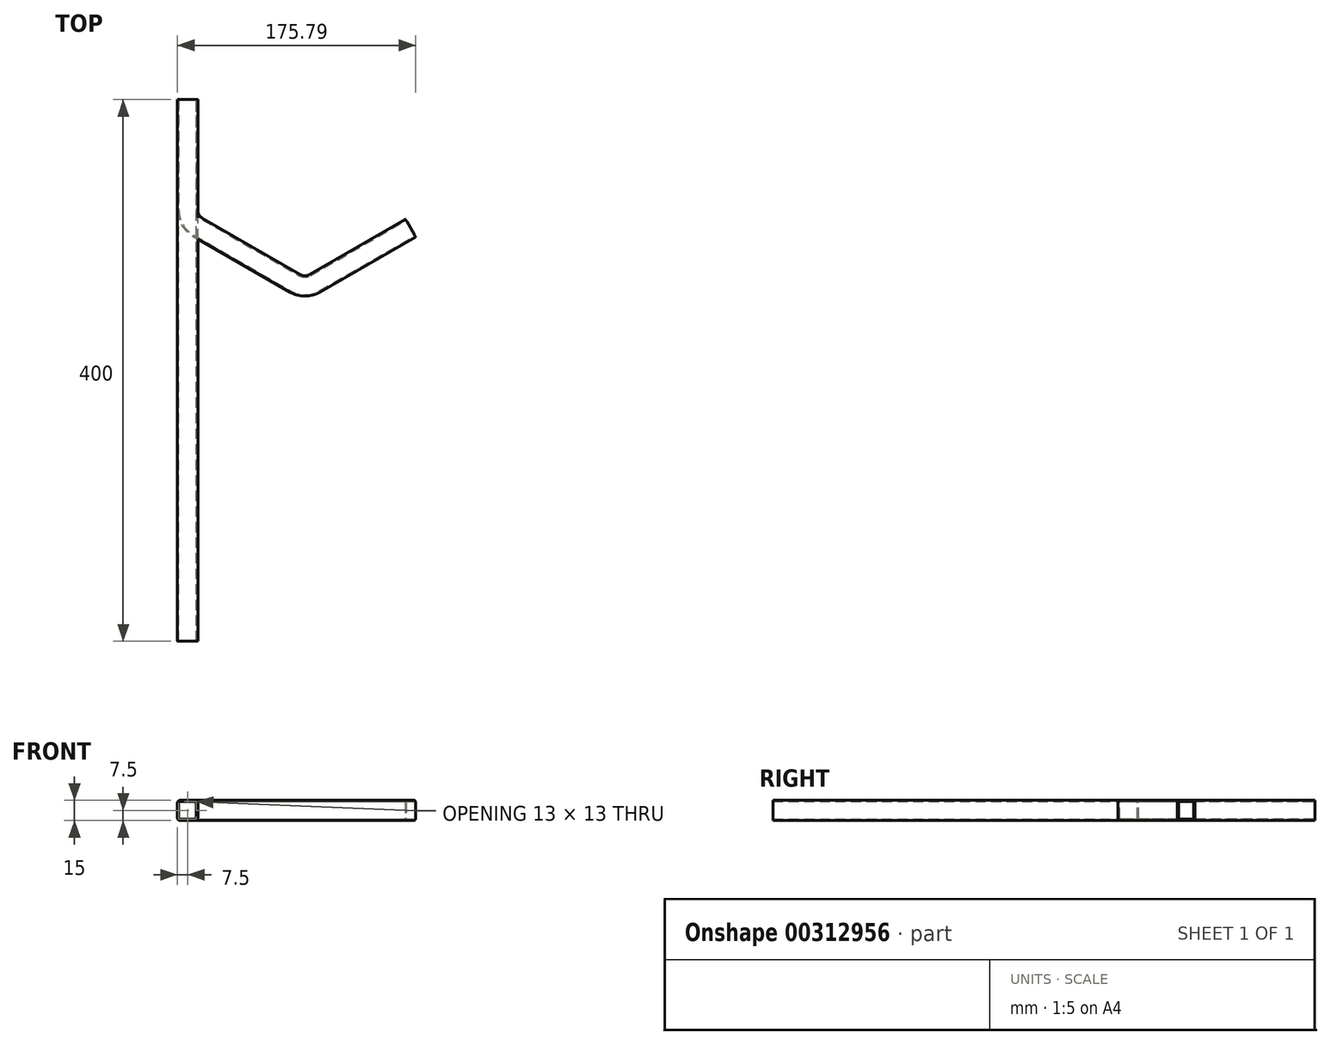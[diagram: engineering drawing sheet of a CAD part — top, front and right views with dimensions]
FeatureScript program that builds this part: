
annotation { "Feature Type Name" : "Feature", "Feature Type Description" : "" }
export const myFeature = defineFeature(function(context is Context, id is Id, definition is map)
    precondition{}
    {
        {
            var Q0;
            Q0=qCreatedBy(makeId("Front.planeOp"),FACE);
            var sketch = newSketch(context, id + "F0", { "sketchPlane" : qUnion([Q0])});
            skLineSegment(sketch, "E0.bottom", {"start": v(5.5, 7.5) * mm, "end": v(-5.5, 7.5) * mm});
            skLineSegment(sketch, "E0.top", {"start": v(5.5, -7.5) * mm, "end": v(-5.5, -7.5) * mm});
            skLineSegment(sketch, "E0.left", {"start": v(7.5, 5.5) * mm, "end": v(7.5, -5.5) * mm});
            skLineSegment(sketch, "E0.right", {"start": v(-7.5, 5.5) * mm, "end": v(-7.5, -5.5) * mm});
            skPoint(sketch, "E0.middle", {"position": v(0, 0) * mm});
            skLineSegment(sketch, "E1.bottom", {"start": v(5.5, 6.5) * mm, "end": v(-5.5, 6.5) * mm});
            skLineSegment(sketch, "E1.top", {"start": v(5.5, -6.5) * mm, "end": v(-5.5, -6.5) * mm});
            skLineSegment(sketch, "E1.left", {"start": v(6.5, 5.5) * mm, "end": v(6.5, -5.5) * mm});
            skLineSegment(sketch, "E1.right", {"start": v(-6.5, 5.5) * mm, "end": v(-6.5, -5.5) * mm});
            skPoint(sketch, "E2.visualSharp", {"position": v(-6.5, 6.5) * mm});
            skArc(sketch, "E2.filletArc", {"start": v(-5.5, 6.5) * mm, "mid": v(-6.2, 6.2) * mm, "end": v(-6.5, 5.5) * mm});
            skPoint(sketch, "E3.visualSharp", {"position": v(6.5, 6.5) * mm});
            skArc(sketch, "E3.filletArc", {"start": v(6.5, 5.5) * mm, "mid": v(6.2, 6.2) * mm, "end": v(5.5, 6.5) * mm});
            skPoint(sketch, "E4.visualSharp", {"position": v(6.5, -6.5) * mm});
            skArc(sketch, "E4.filletArc", {"start": v(5.5, -6.5) * mm, "mid": v(6.2, -6.2) * mm, "end": v(6.5, -5.5) * mm});
            skPoint(sketch, "E5.visualSharp", {"position": v(-6.5, -6.5) * mm});
            skArc(sketch, "E5.filletArc", {"start": v(-6.5, -5.5) * mm, "mid": v(-6.2, -6.2) * mm, "end": v(-5.5, -6.5) * mm});
            skPoint(sketch, "E6.visualSharp", {"position": v(-7.5, 7.5) * mm});
            skArc(sketch, "E6.filletArc", {"start": v(-5.5, 7.5) * mm, "mid": v(-6.91, 6.91) * mm, "end": v(-7.5, 5.5) * mm});
            skPoint(sketch, "E7.visualSharp", {"position": v(7.5, 7.5) * mm});
            skArc(sketch, "E7.filletArc", {"start": v(7.5, 5.5) * mm, "mid": v(6.91, 6.91) * mm, "end": v(5.5, 7.5) * mm});
            skPoint(sketch, "E8.visualSharp", {"position": v(7.5, -7.5) * mm});
            skArc(sketch, "E8.filletArc", {"start": v(5.5, -7.5) * mm, "mid": v(6.91, -6.91) * mm, "end": v(7.5, -5.5) * mm});
            skPoint(sketch, "E9.visualSharp", {"position": v(-7.5, -7.5) * mm});
            skArc(sketch, "E9.filletArc", {"start": v(-7.5, -5.5) * mm, "mid": v(-6.91, -6.91) * mm, "end": v(-5.5, -7.5) * mm});
            skSolve(sketch);
        }
        {
            var Q0;
            Q0 = qSketchRegion(id + "F0", true);
            extrude(context, id + "F1", {"entities" : qUnion([Q0]), "depth" : 400 * mm, "offsetDistance" : 25 * mm});
        }
        {
            var Q0;
            Q0=qCreatedBy(makeId("Top.planeOp"),FACE);
            var sketch = newSketch(context, id + "F2", { "sketchPlane" : qUnion([Q0])});
            skLineSegment(sketch, "E10", {"start": v(0, 0) * mm, "end": v(0, -81.34) * mm});
            skLineSegment(sketch, "E11", {"start": v(7.5, -94.33) * mm, "end": v(79.1, -135.67) * mm});
            skLineSegment(sketch, "E12", {"start": v(94.1, -135.67) * mm, "end": v(164.54, -95) * mm});
            skPoint(sketch, "E13.visualSharp", {"position": v(86.6, -140) * mm});
            skArc(sketch, "E13.filletArc", {"start": v(79.1, -135.67) * mm, "mid": v(86.6, -137.68) * mm, "end": v(94.1, -135.67) * mm});
            skPoint(sketch, "E14.visualSharp", {"position": v(0, -90) * mm});
            skArc(sketch, "E14.filletArc", {"start": v(0, -81.34) * mm, "mid": v(2, -88.84) * mm, "end": v(7.5, -94.33) * mm});
            skSolve(sketch);
        }
        {
            var Q0;
            Q0=makeQuery(id+"F1.opExtrude","CAP_FACE",FACE,{"disambiguationData":[OSD([sQuery(id+"F0.wireOp",EDGE,"E0.bottom"),sQuery(id+"F0.wireOp",EDGE,"E0.top"),sQuery(id+"F0.wireOp",EDGE,"E0.left"),sQuery(id+"F0.wireOp",EDGE,"E0.right"),sQuery(id+"F0.wireOp",EDGE,"E1.bottom"),sQuery(id+"F0.wireOp",EDGE,"E1.top"),sQuery(id+"F0.wireOp",EDGE,"E1.left"),sQuery(id+"F0.wireOp",EDGE,"E1.right"),sQuery(id+"F0.wireOp",EDGE,"E2.filletArc"),sQuery(id+"F0.wireOp",EDGE,"E3.filletArc"),sQuery(id+"F0.wireOp",EDGE,"E4.filletArc"),sQuery(id+"F0.wireOp",EDGE,"E5.filletArc"),sQuery(id+"F0.wireOp",EDGE,"E6.filletArc"),sQuery(id+"F0.wireOp",EDGE,"E7.filletArc"),sQuery(id+"F0.wireOp",EDGE,"E8.filletArc"),sQuery(id+"F0.wireOp",EDGE,"E9.filletArc")])],"isStart":true});
            var Q1;
            Q1 = qConstructionFilter(qBodyType(qCreatedBy(id + "F2" ,EDGE), BodyType.WIRE), ConstructionObject.NO);
            sweep(context, id + "F3", {"profiles" : qUnion([Q0]), "path" : qUnion([Q1])});
        }
    });
